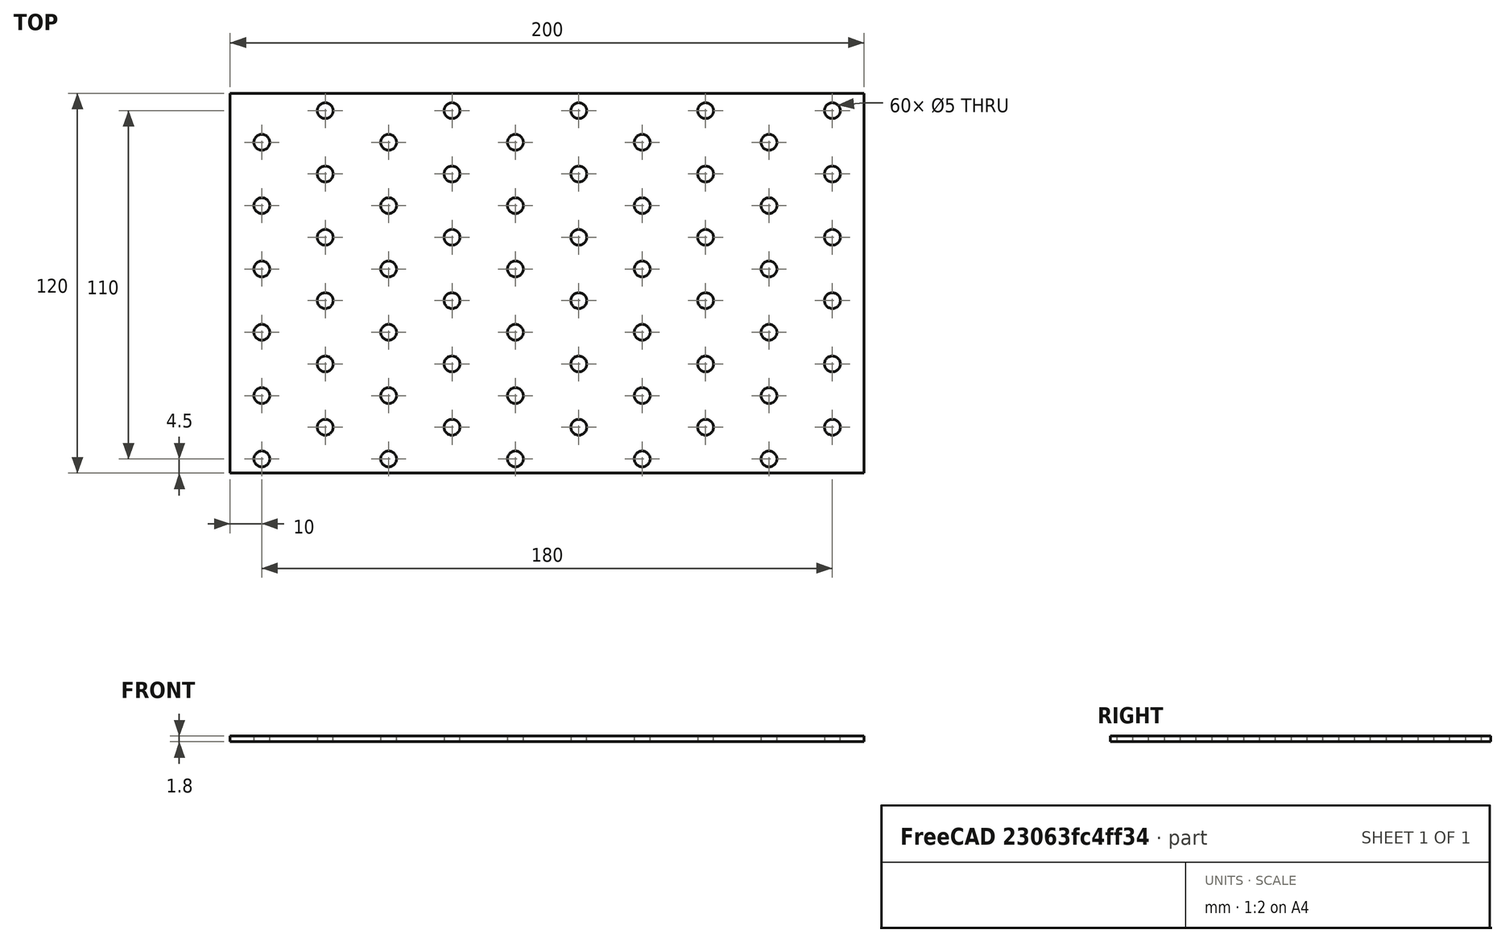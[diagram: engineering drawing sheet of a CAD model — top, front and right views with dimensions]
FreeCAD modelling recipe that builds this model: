
FCSTD DOCUMENT  (FreeCAD 0.19R24276 (Git))
Label: Bar_120x200__1_8mm_Master_Skerch_for_Bear_90x140
License: All rights reserved
LicenseURL: http://en.wikipedia.org/wiki/All_rights_reserved
objects: Sketcher::SketchObject×1, PartDesign::Pad×1, PartDesign::Body×1
note: 4 computed .brp shape members not serialized (recipe doc carries the construction recipe); baked Part::Feature solids carry a one-line shape summary decoded from their .brp

FEATURE [Sketcher::SketchObject] Sketch
  FullyConstrained = false
  MapMode = 5
  Support = -> [XY_Plane]
  sketch-geometry (72):
    g0: Circle CenterX=0 CenterY=0 CenterZ=0 NormalX=0 NormalY=0 NormalZ=1 AngleXU=0 Radius=2.5
    g1: Circle CenterX=0 CenterY=20 CenterZ=0 NormalX=0 NormalY=0 NormalZ=1 AngleXU=0 Radius=2.5
    g2: Circle CenterX=0 CenterY=40 CenterZ=0 NormalX=0 NormalY=0 NormalZ=1 AngleXU=0 Radius=2.5
    g3: Circle CenterX=0 CenterY=60 CenterZ=0 NormalX=0 NormalY=0 NormalZ=1 AngleXU=0 Radius=2.5
    g4: Circle CenterX=20 CenterY=10 CenterZ=0 NormalX=0 NormalY=0 NormalZ=1 AngleXU=0 Radius=2.5
    g5: Circle CenterX=20 CenterY=30 CenterZ=0 NormalX=0 NormalY=0 NormalZ=1 AngleXU=0 Radius=2.5
    g6: Circle CenterX=20 CenterY=50 CenterZ=0 NormalX=0 NormalY=0 NormalZ=1 AngleXU=0 Radius=2.5
    g7: Circle CenterX=20 CenterY=70 CenterZ=0 NormalX=0 NormalY=0 NormalZ=1 AngleXU=0 Radius=2.5
    g8: Circle CenterX=40 CenterY=0 CenterZ=0 NormalX=0 NormalY=0 NormalZ=1 AngleXU=0 Radius=2.5
    g9: Circle CenterX=40 CenterY=20 CenterZ=0 NormalX=0 NormalY=0 NormalZ=1 AngleXU=0 Radius=2.5
    g10: Circle CenterX=40 CenterY=40 CenterZ=0 NormalX=0 NormalY=0 NormalZ=1 AngleXU=0 Radius=2.5
    g11: Circle CenterX=40 CenterY=60 CenterZ=0 NormalX=0 NormalY=0 NormalZ=1 AngleXU=0 Radius=2.5
    g12: Circle CenterX=60 CenterY=10 CenterZ=0 NormalX=0 NormalY=0 NormalZ=1 AngleXU=0 Radius=2.5
    g13: Circle CenterX=60 CenterY=30 CenterZ=0 NormalX=0 NormalY=0 NormalZ=1 AngleXU=0 Radius=2.5
    g14: Circle CenterX=60 CenterY=50 CenterZ=0 NormalX=0 NormalY=0 NormalZ=1 AngleXU=0 Radius=2.5
    g15: Circle CenterX=60 CenterY=70 CenterZ=0 NormalX=0 NormalY=0 NormalZ=1 AngleXU=0 Radius=2.5
    g16: Circle CenterX=80 CenterY=0 CenterZ=0 NormalX=0 NormalY=0 NormalZ=1 AngleXU=0 Radius=2.5
    g17: Circle CenterX=80 CenterY=20 CenterZ=0 NormalX=0 NormalY=0 NormalZ=1 AngleXU=0 Radius=2.5
    g18: Circle CenterX=80 CenterY=40 CenterZ=0 NormalX=0 NormalY=0 NormalZ=1 AngleXU=0 Radius=2.5
    g19: Circle CenterX=80 CenterY=60 CenterZ=0 NormalX=0 NormalY=0 NormalZ=1 AngleXU=0 Radius=2.5
    g20: Circle CenterX=100 CenterY=10 CenterZ=0 NormalX=0 NormalY=0 NormalZ=1 AngleXU=0 Radius=2.5
    g21: Circle CenterX=100 CenterY=30 CenterZ=0 NormalX=0 NormalY=0 NormalZ=1 AngleXU=0 Radius=2.5
    g22: Circle CenterX=100 CenterY=50 CenterZ=0 NormalX=0 NormalY=0 NormalZ=1 AngleXU=0 Radius=2.5
    g23: Circle CenterX=100 CenterY=70 CenterZ=0 NormalX=0 NormalY=0 NormalZ=1 AngleXU=0 Radius=2.5
    g24: Circle CenterX=120 CenterY=0 CenterZ=0 NormalX=0 NormalY=0 NormalZ=1 AngleXU=0 Radius=2.5
    g25: Circle CenterX=120 CenterY=20 CenterZ=0 NormalX=0 NormalY=0 NormalZ=1 AngleXU=0 Radius=2.5
    g26: Circle CenterX=120 CenterY=40 CenterZ=0 NormalX=0 NormalY=0 NormalZ=1 AngleXU=0 Radius=2.5
    g27: Circle CenterX=120 CenterY=60 CenterZ=0 NormalX=0 NormalY=0 NormalZ=1 AngleXU=0 Radius=2.5
    g28: Circle CenterX=140 CenterY=10 CenterZ=0 NormalX=0 NormalY=0 NormalZ=1 AngleXU=0 Radius=2.5
    g29: Circle CenterX=140 CenterY=30 CenterZ=0 NormalX=0 NormalY=0 NormalZ=1 AngleXU=0 Radius=2.5
    g30: Circle CenterX=140 CenterY=50 CenterZ=0 NormalX=0 NormalY=0 NormalZ=1 AngleXU=0 Radius=2.5
    g31: Circle CenterX=140 CenterY=70 CenterZ=0 NormalX=0 NormalY=0 NormalZ=1 AngleXU=0 Radius=2.5
    g32: LineSegment StartX=-10 StartY=115.5 StartZ=0 EndX=190 EndY=115.5 EndZ=0
    g33: LineSegment StartX=190 StartY=115.5 StartZ=0 EndX=190 EndY=-4.5 EndZ=0
    g34: LineSegment StartX=190 StartY=-4.5 StartZ=0 EndX=-10 EndY=-4.5 EndZ=0
    g35: LineSegment StartX=-10 StartY=-4.5 StartZ=0 EndX=-10 EndY=115.5 EndZ=0
    g36: Circle CenterX=160 CenterY=0 CenterZ=0 NormalX=0 NormalY=0 NormalZ=1 AngleXU=0 Radius=2.5
    g37: Circle CenterX=160 CenterY=20 CenterZ=0 NormalX=0 NormalY=0 NormalZ=1 AngleXU=0 Radius=2.5
    g38: Circle CenterX=160 CenterY=40 CenterZ=0 NormalX=0 NormalY=0 NormalZ=1 AngleXU=0 Radius=2.5
    g39: Circle CenterX=160 CenterY=60 CenterZ=0 NormalX=0 NormalY=0 NormalZ=1 AngleXU=0 Radius=2.5
    g40: Circle CenterX=180 CenterY=10 CenterZ=0 NormalX=0 NormalY=0 NormalZ=1 AngleXU=0 Radius=2.5
    g41: Circle CenterX=180 CenterY=30 CenterZ=0 NormalX=0 NormalY=0 NormalZ=1 AngleXU=0 Radius=2.5
    g42: Circle CenterX=180 CenterY=50 CenterZ=0 NormalX=0 NormalY=0 NormalZ=1 AngleXU=0 Radius=2.5
    g43: Circle CenterX=180 CenterY=70 CenterZ=0 NormalX=0 NormalY=0 NormalZ=1 AngleXU=0 Radius=2.5
    g44: Circle CenterX=1.8e-15 CenterY=80 CenterZ=0 NormalX=0 NormalY=0 NormalZ=1 AngleXU=0 Radius=2.5
    g45: Circle CenterX=20 CenterY=90 CenterZ=0 NormalX=0 NormalY=0 NormalZ=1 AngleXU=0 Radius=2.5
    g46: Circle CenterX=40 CenterY=80 CenterZ=0 NormalX=0 NormalY=0 NormalZ=1 AngleXU=0 Radius=2.5
    g47: Circle CenterX=60 CenterY=90 CenterZ=0 NormalX=0 NormalY=0 NormalZ=1 AngleXU=0 Radius=2.5
    g48: Circle CenterX=80 CenterY=80 CenterZ=0 NormalX=0 NormalY=0 NormalZ=1 AngleXU=0 Radius=2.5
    g49: Circle CenterX=100 CenterY=90 CenterZ=0 NormalX=0 NormalY=0 NormalZ=1 AngleXU=0 Radius=2.5
    g50: Circle CenterX=120 CenterY=80 CenterZ=0 NormalX=0 NormalY=0 NormalZ=1 AngleXU=0 Radius=2.5
    g51: Circle CenterX=140 CenterY=90 CenterZ=0 NormalX=0 NormalY=0 NormalZ=1 AngleXU=0 Radius=2.5
    g52: Circle CenterX=160 CenterY=80 CenterZ=0 NormalX=0 NormalY=0 NormalZ=1 AngleXU=0 Radius=2.5
    g53: Circle CenterX=180 CenterY=90 CenterZ=0 NormalX=0 NormalY=0 NormalZ=1 AngleXU=0 Radius=2.5
    g54: Circle CenterX=1.8e-15 CenterY=100 CenterZ=0 NormalX=0 NormalY=0 NormalZ=1 AngleXU=0 Radius=2.5
    g55: Circle CenterX=40 CenterY=100 CenterZ=0 NormalX=0 NormalY=0 NormalZ=1 AngleXU=0 Radius=2.5
    g56: Circle CenterX=80 CenterY=100 CenterZ=0 NormalX=0 NormalY=0 NormalZ=1 AngleXU=0 Radius=2.5
    g57: Circle CenterX=120 CenterY=100 CenterZ=0 NormalX=0 NormalY=0 NormalZ=1 AngleXU=0 Radius=2.5
    g58: Circle CenterX=160 CenterY=100 CenterZ=0 NormalX=0 NormalY=0 NormalZ=1 AngleXU=0 Radius=2.5
    g59: Circle CenterX=20 CenterY=110 CenterZ=0 NormalX=0 NormalY=0 NormalZ=1 AngleXU=0 Radius=2.5
    g60: Circle CenterX=60 CenterY=110 CenterZ=0 NormalX=0 NormalY=0 NormalZ=1 AngleXU=0 Radius=2.5
    g61: Circle CenterX=100 CenterY=110 CenterZ=0 NormalX=0 NormalY=0 NormalZ=1 AngleXU=0 Radius=2.5
    g62: Circle CenterX=140 CenterY=110 CenterZ=0 NormalX=0 NormalY=0 NormalZ=1 AngleXU=0 Radius=2.5
    g63: Circle CenterX=180 CenterY=110 CenterZ=0 NormalX=0 NormalY=0 NormalZ=1 AngleXU=0 Radius=2.5
    g64: LineSegment StartX=90 StartY=115.5 StartZ=0 EndX=90 EndY=-4.5 EndZ=0
    g65: LineSegment StartX=-10 StartY=55.5 StartZ=0 EndX=190 EndY=55.5 EndZ=0
    g66: Circle CenterX=90 CenterY=55.5 CenterZ=0 NormalX=0 NormalY=0 NormalZ=1 AngleXU=0 Radius=4.35123
    g67: Circle CenterX=90 CenterY=55.5 CenterZ=0 NormalX=0 NormalY=0 NormalZ=1 AngleXU=0 Radius=78.5
    g68: LineSegment StartX=34.4921 StartY=111.008 StartZ=0 EndX=145.508 EndY=-0.00788232 EndZ=0
    g69: LineSegment StartX=34.4921 StartY=-0.00788232 StartZ=0 EndX=90 EndY=55.5 EndZ=0
    g70: Circle CenterX=90 CenterY=55.5 CenterZ=0 NormalX=0 NormalY=0 NormalZ=1 AngleXU=0 Radius=78.5
    g71: LineSegment StartX=90 StartY=55.5 StartZ=0 EndX=145.508 EndY=111.008 EndZ=0
  constraints (211):
    c: Coincident(g0,g-1)
    c: PointOnObject(g1,g-2)
    c: PointOnObject(g2,g-2)
    c: PointOnObject(g3,g-2)
    c: Diameter(g0) = 5
    c: Equal(g0,g1)
    c: Equal(g0,g2)
    c: Equal(g0,g3)
    c: DistanceY(g0,g1) = 20
    c: DistanceY(g1,g2) = 20
    c: DistanceY(g2,g3) = 20
    c: Equal(g0,g4) = 5
    c: Equal(g4,g5)
    c: Equal(g4,g6)
    c: Equal(g4,g7)
    c: DistanceY(g4,g5) = 20
    c: DistanceY(g5,g6) = 20
    c: DistanceY(g6,g7) = 20
    c: DistanceY(g0,g4) = 10
    c: DistanceX(g0,g4) = 20
    c: DistanceX(g5,g4) = 0
    c: DistanceX(g6,g5) = 0
    c: DistanceX(g7,g6) = 0
    c: Equal(g0,g8) = 5
    c: Equal(g8,g9)
    c: Equal(g8,g10)
    c: Equal(g8,g11)
    c: DistanceY(g8,g9) = 20
    c: DistanceY(g9,g10) = 20
    c: DistanceY(g10,g11) = 20
    c: Equal(g8,g12) = 5
    c: Equal(g12,g13)
    c: Equal(g12,g14)
    c: Equal(g12,g15)
    c: DistanceY(g12,g13) = 20
    c: DistanceY(g13,g14) = 20
    c: DistanceY(g14,g15) = 20
    c: DistanceY(g8,g12) = 10
    c: DistanceX(g8,g12) = 20
    c: DistanceX(g13,g12) = 0
    c: DistanceX(g14,g13) = 0
    c: DistanceX(g15,g14) = 0
    c: DistanceY(g8,g0) = 0
    c: DistanceX(g9,g8) = 0
    c: DistanceX(g9,g10) = 0
    c: DistanceX(g11,g10) = 0
    c: DistanceX(g4,g8) = 20
    c: Equal(g0,g16) = 5
    c: Equal(g16,g17)
    c: Equal(g16,g18)
    c: Equal(g16,g19)
    c: DistanceY(g16,g17) = 20
    c: DistanceY(g17,g18) = 20
    c: DistanceY(g18,g19) = 20
    c: Equal(g16,g20) = 5
    c: Equal(g20,g21)
    c: Equal(g20,g22)
    c: Equal(g20,g23)
    c: DistanceY(g20,g21) = 20
    c: DistanceY(g21,g22) = 20
    c: DistanceY(g22,g23) = 20
    c: DistanceY(g16,g20) = 10
    c: DistanceX(g16,g20) = 20
    c: DistanceX(g21,g20) = 0
    c: DistanceX(g22,g21) = 0
    c: DistanceX(g23,g22) = 0
    c: Equal(g16,g24) = 5
    c: Equal(g24,g25)
    c: Equal(g24,g26)
    c: Equal(g24,g27)
    c: DistanceY(g24,g25) = 20
    c: DistanceY(g25,g26) = 20
    c: DistanceY(g26,g27) = 20
    c: Equal(g24,g28) = 5
    c: Equal(g28,g29)
    c: Equal(g28,g30)
    c: Equal(g28,g31)
    c: DistanceY(g28,g29) = 20
    c: DistanceY(g29,g30) = 20
    c: DistanceY(g30,g31) = 20
    c: DistanceY(g24,g28) = 10
    c: DistanceX(g24,g28) = 20
    c: DistanceX(g29,g28) = 0
    c: DistanceX(g30,g29) = 0
    c: DistanceX(g31,g30) = 0
    c: DistanceY(g24,g16) = 0
    c: DistanceX(g25,g24) = 0
    c: DistanceX(g25,g26) = 0
    c: DistanceX(g27,g26) = 0
    c: DistanceX(g20,g24) = 20
    c: DistanceX(g16,g17) = 0
    c: DistanceX(g17,g18) = 0
    c: DistanceX(g18,g19) = 0
    c: DistanceX(g12,g16) = 20
    c: DistanceY(g8,g16) = 0
    c: Coincident(g32,g33)
    c: Coincident(g33,g34)
    c: Coincident(g34,g35)
    c: Horizontal(g32)
    c: Horizontal(g34)
    c: Vertical(g33)
    c: Vertical(g35)
    c: DistanceY(g33,g33) = 120
    c: DistanceY(g34,g0) = 4.5
    c: DistanceX(g34,g0) = 10
    c: Equal(g36,g37)
    c: Equal(g36,g38)
    c: Equal(g36,g39)
    c: DistanceY(g36,g37) = 20
    c: DistanceY(g37,g38) = 20
    c: DistanceY(g38,g39) = 20
    c: Equal(g36,g40) = 5
    c: Equal(g40,g41)
    c: Equal(g40,g42)
    c: Equal(g40,g43)
    c: DistanceY(g40,g41) = 20
    c: DistanceY(g41,g42) = 20
    c: DistanceY(g42,g43) = 20
    c: DistanceY(g36,g40) = 10
    c: DistanceX(g36,g40) = 20
    c: DistanceX(g41,g40) = 0
    c: DistanceX(g42,g41) = 0
    c: DistanceX(g43,g42) = 0
    c: DistanceX(g37,g36) = 0
    c: DistanceX(g37,g38) = 0
    c: DistanceX(g39,g38) = 0
    c: DistanceY(g36,g24) = 0
    c: DistanceX(g28,g36) = 20
    c: Equal(g0,g44) = 5
    c: Equal(g44,g45) = 5
    c: DistanceY(g44,g45) = 10
    c: DistanceX(g44,g45) = 20
    c: Equal(g44,g46) = 5
    c: Equal(g46,g47) = 5
    c: DistanceY(g46,g47) = 10
    c: DistanceX(g46,g47) = 20
    c: DistanceY(g46,g44) = 0
    c: DistanceX(g45,g46) = 20
    c: Equal(g44,g48) = 5
    c: Equal(g48,g49) = 5
    c: DistanceY(g48,g49) = 10
    c: DistanceX(g48,g49) = 20
    c: Equal(g48,g50) = 5
    c: Equal(g50,g51) = 5
    c: DistanceY(g50,g51) = 10
    c: DistanceX(g50,g51) = 20
    c: DistanceY(g50,g48) = 0
    c: DistanceX(g49,g50) = 20
    c: DistanceX(g47,g48) = 20
    c: DistanceY(g46,g48) = 0
    c: Equal(g52,g53) = 5
    c: DistanceY(g52,g53) = 10
    c: DistanceX(g52,g53) = 20
    c: DistanceY(g52,g50) = 0
    c: DistanceX(g51,g52) = 20
    c: DistanceX(g53,g43) = 0
    c: DistanceY(g43,g52) = 10
    c: DistanceX(g34,g34) = 200
    c: PointOnObject(g35,g32)
    c: Equal(g54,g59) = 5
    c: DistanceY(g54,g59) = 10
    c: DistanceX(g54,g59) = 20
    c: Equal(g54,g55) = 5
    c: Equal(g55,g60) = 5
    c: DistanceY(g55,g60) = 10
    c: DistanceX(g55,g60) = 20
    c: DistanceY(g55,g54) = 0
    c: DistanceX(g59,g55) = 20
    c: Equal(g54,g56) = 5
    c: Equal(g56,g61) = 5
    c: DistanceY(g56,g61) = 10
    c: DistanceX(g56,g61) = 20
    c: Equal(g56,g57) = 5
    c: Equal(g57,g62) = 5
    c: DistanceY(g57,g62) = 10
    c: DistanceX(g57,g62) = 20
    c: DistanceY(g57,g56) = 0
    c: DistanceX(g61,g57) = 20
    c: DistanceX(g60,g56) = 20
    c: DistanceY(g55,g56) = 0
    c: Equal(g58,g63) = 5
    c: DistanceY(g58,g63) = 10
    c: DistanceX(g58,g63) = 20
    c: DistanceY(g58,g57) = 0
    c: DistanceX(g62,g58) = 20
    c: DistanceX(g44,g54) = 0
    c: DistanceY(g45,g54) = 10
    c: Vertical(g64)
    c: Horizontal(g65)
    c: PointOnObject(g65,g33)
    c: PointOnObject(g64,g32)
    c: PointOnObject(g64,g34)
    c: PointOnObject(g65,g35)
    c: DistanceY(g33,g65) = 60
    c: DistanceX(g34,g64) = 100
    c: DistanceX(g64,g66) = 0
    c: DistanceY(g65,g66) = 0
    c: Coincident(g67,g66)
    c: Diameter(g67) = 157
    c: PointOnObject(g69,g68)
    c: Coincident(g70,g69)
    c: Coincident(g71,g69)
    c: Angle(g68,g71) = 1.5708
    c: Angle(g69,g68) = 1.5708
    c: Diameter(g70) = 157
    c: Coincident(g66,g69)
    c: PointOnObject(g71,g67)
    c: PointOnObject(g68,g67)
    c: PointOnObject(g68,g67)
    c: PointOnObject(g69,g67)
    c: Angle(g71,g65) = 2.35619
FEATURE [PartDesign::Pad] Pad
  Direction = (1,1,1)
  Length = 1.8
  Length2 = 100
  Profile = -> Sketch
  Type = 0
FEATURE [PartDesign::Body] Body
  Group = -> [Sketch,Pad]
  Origin = -> Origin
  Tip = -> Pad
